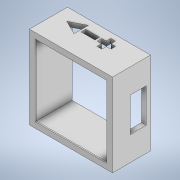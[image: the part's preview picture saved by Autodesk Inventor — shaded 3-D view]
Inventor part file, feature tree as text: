
AUTODESK INVENTOR PART (.ipt)
format: ipt  version: 2020.1 (Build 241239000, 239)  size: 222,208 bytes
history: native  units: in
note: dims shown in document units (in); Inventor stores cm internally (conversion verified against a paired STEP export)
features: extrude x9, sketch x8
ambient origin geometry x8: Origin, YZ Plane, XZ Plane, XY Plane, X Axis, Y Axis, Z Axis, Center Point
bodies: Solid1 (feature_tree)
feature tree (17):
  extrude  "Extrusion1"  Depth=2.874in
  extrude  "Extrusion2"  Depth=0.1575in
  extrude  "Extrusion3"  Depth=0.0394in
  extrude  "Extrusion4"  Depth=0.0394in TaperAngle=0.0deg
  extrude  "Extrusion5"  Depth=0.5512in
  extrude  "Extrusion6"  Depth=0.1575in TaperAngle=0.0deg
  sketch  "Sketch10"  dims[d53=0.1575in d54=0.0in d93=0.1575in d94=0.0in]
  extrude  "Extrusion8"  Depth=0.1575in TaperAngle=0.0deg
  extrude  "Extrusion9"  Depth=0.0197in
  extrude  "Extrusion10"  Depth=0.0197in
  sketch  "Sketch2"  dims[d2=2.874in d3=2.874in]
  sketch  "Sketch3"  dims[d4=0.7874in d5=0.0in d6=0.1575in]
  sketch  "Sketch4"  dims[d7=0.7874in d8=0.0in d9=0.0394in]
  sketch  "Sketch5"  dims[d10=0.0394in d11=0.0in d12=0.5315in d13=0.0in]
  sketch  "Sketch7"  dims[d43=0.5906in d44=0.5512in]
  sketch  "Sketch8"  dims[d45=1.1811in d46=0.1575in d47=0.0in]
  sketch  "Sketch11"  dims[d95=0.0039in d96=0.0039in d97=0.0039in d98=0.1575in d99=0.0in d100=0.0984in d101=0.1181in d102=0.0984in d103=0.0984in d104=0.1181in d105=0.0in d106=0.1969in d42=0.0197in]
